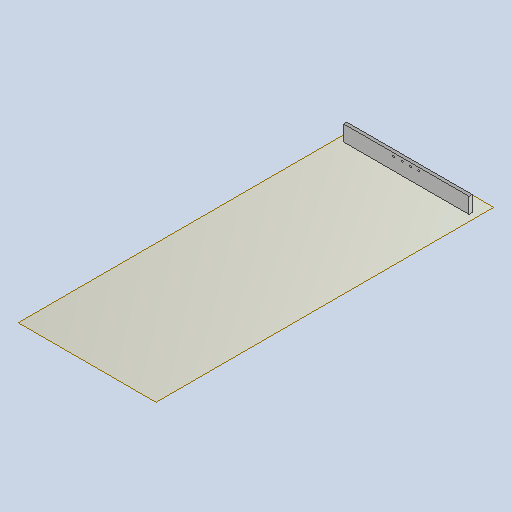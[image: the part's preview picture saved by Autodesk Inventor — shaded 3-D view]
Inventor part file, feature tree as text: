
AUTODESK INVENTOR PART (.ipt)
format: ipt  version: 2025 (Build 290162010, 162A)  size: 164,864 bytes
history: native  units: mm
features: other x3, sketch x2, plane x1, extrude x1, hole x1, reference x1
ambient origin geometry x8: Origin, YZ Plane, XZ Plane, XY Plane, X Axis, Y Axis, Z Axis, Center Point
bodies: Volumenkörper1 (feature_tree)
feature tree (9):
  plane  "Arbeitsebene1"
  extrude  "Extrusion1"  Depth=25.0mm TaperAngle=0.0deg
  hole  "Bohrung1"  [1 undecoded]
  sketch  "Skizze1"  dims[d0=5.0mm d1=25.0mm d2=0.0mm]
  reference  "Referenz1"
  sketch  "Skizze2"  dims[d3=3.0mm d4=8.0mm d5=4.0mm d6=2.0mm d7=90.0deg d8=10.0mm d9=20.594885mm d10=0.5mm d11=0.872665mm d12=0.5mm d13=0.872665mm]
  other  "<userpath>\Documents\Inventor\Krandemonstrator\Demonstrator.iam"
  other  "Demonstrator.iam"
  other  "FrameSide:1"
note: 1 required parameter value undecoded (feature->parameter linkage not recoverable at this tier; creation-order binding heuristic only, values carry confidence <= 0.55)
